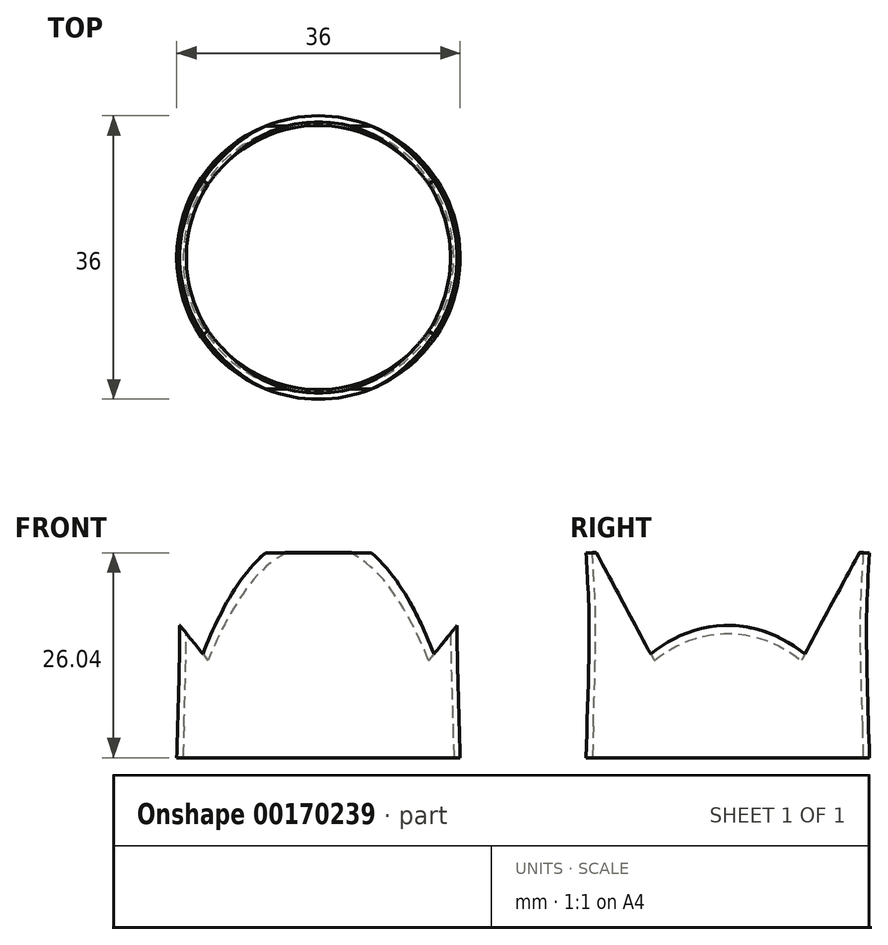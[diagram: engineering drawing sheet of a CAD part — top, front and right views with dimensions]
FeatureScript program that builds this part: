
annotation { "Feature Type Name" : "Feature", "Feature Type Description" : "" }
export const myFeature = defineFeature(function(context is Context, id is Id, definition is map)
    precondition{}
    {
        {
            assignVariable(context, id + "F0", {"name" : "cop", "anyValue" : 5});
        }
        {
            var Q0;
            Q0=qCreatedBy(makeId("Top.planeOp"),FACE);
            var sketch = newSketch(context, id + "F1", { "sketchPlane" : qUnion([Q0])});
            skCircle(sketch, "E0", {"center": v(0, 0) * mm, "radius": 16 * mm});
            skCircle(sketch, "E1.0", {"center": v(0, 0) * mm, "radius": 18 * mm});
            skSolve(sketch);
        }
        {
            var Q0;
            Q0=qCreatedBy(makeId("Front.planeOp"),FACE);
            var sketch = newSketch(context, id + "F2", { "sketchPlane" : qUnion([Q0])});
            skLineSegment(sketch, "E2.0", {"start": v(-18, 0) * mm, "end": v(18, 0) * mm});
            skLineSegment(sketch, "E3.0", {"start": v(-16, 0) * mm, "end": v(16, 0) * mm});
            skFitSpline(sketch, "E4", {"points": [v(18, 0) * mm, v(18, 26) * mm], "startDerivative": vector(-1.55, 51.63) * mm, "endDerivative": vector(1.55, 26.7) * mm});
            skFitSpline(sketch, "E5.0", {"points": [v(17.2, -0.02) * mm, v(17.07, 4.28) * mm, v(16.88, 10.72) * mm, v(16.78, 16.37) * mm, v(16.88, 20.5) * mm, v(17.07, 23.82) * mm, v(17.2, 26.05) * mm]});
            skLineSegment(sketch, "E6", {"start": v(17.2, 26.04) * mm, "end": v(18, 26) * mm});
            skLineSegment(sketch, "E7", {"start": v(17.14, 2) * mm, "end": v(16, 2) * mm});
            skLineSegment(sketch, "E8", {"start": v(16, 2) * mm, "end": v(16.56, 0) * mm});
            skLineSegment(sketch, "E9", {"start": v(16, 2) * mm, "end": v(16, 4) * mm});
            skLineSegment(sketch, "E10", {"start": v(16, 4) * mm, "end": v(17.08, 4) * mm});
            skSolve(sketch);
        }
        {
            var Q0;
            {var subQ0=sQuery(id+"F2.wireOp",EDGE,"E4");Q0=makeQuery(id+"F2.imprint","IMPRINT",FACE,{"disambiguationData":[TD([[makeQuery(id+"F2.imprint","IMPRINT",EDGE,{"derivedFrom":subQ0}),1.0]])]});}
            var Q1;
            {var subQ4=sQuery(id+"F2.wireOp",EDGE,"E7");Q1=makeQuery(id+"F2.imprint","IMPRINT",FACE,{"disambiguationData":[TD([[makeQuery(id+"F2.imprint","IMPRINT",EDGE,{"derivedFrom":subQ4}),1.0]])]});}
            var Q2;
            {var subQ0=sQuery(id+"F2.wireOp",EDGE,"E7");Q2=makeQuery(id+"F2.imprint","IMPRINT",FACE,{"disambiguationData":[TD([[makeQuery(id+"F2.imprint","IMPRINT",EDGE,{"derivedFrom":subQ0}),-1.0]])]});}
            var Q3;
            Q3=sQuery(id+"F1.wireOp",EDGE,"E0");
            revolve(context, id + "F3", {"entities" : qUnion([Q0, Q1, Q2]), "axis" : qUnion([Q3]), "revolveType" : RevolveType.FULL});
        }
        {
            var Q0;
            Q0=qCreatedBy(makeId("Top.planeOp"),FACE);
            cPlane(context, id + "F4", {"entities" : qUnion([Q0]), "cplaneType" : CPlaneType.OFFSET, "offset" : (getVariable(context, 'cop')) * mm, "oppositeDirection" : true, "width" : 150 * mm, "height" : 150 * mm});
        }
        {
            var Q0;
            Q0=qCreatedBy(id+"F4.planeOp",FACE);
            var sketch = newSketch(context, id + "F5", { "sketchPlane" : qUnion([Q0])});
            skCircle(sketch, "E11.0", {"center": v(0, 0) * mm, "radius": 16 * mm});
            skPoint(sketch, "E12.right.end.orphan", {"position": v(-0.75, 0.5) * mm});
            skPoint(sketch, "E12.bottom.end.orphan", {"position": v(-0.75, -0.5) * mm});
            skPoint(sketch, "E12.left.end.orphan", {"position": v(0.75, 0.5) * mm});
            skPoint(sketch, "E12.left.start.orphan", {"position": v(0.75, -0.5) * mm});
            skSolve(sketch);
        }
        {
            var Q0;
            Q0=qCreatedBy(id+"F4.planeOp",FACE);
            cPlane(context, id + "F6", {"entities" : qUnion([Q0]), "cplaneType" : CPlaneType.OFFSET, "offset" : (100 - getVariable(context, 'cop')) * mm, "width" : 150 * mm, "height" : 150 * mm});
        }
        {
            var Q0;
            Q0=qCreatedBy(id+"F6.planeOp",FACE);
            var sketch = newSketch(context, id + "F7", { "sketchPlane" : qUnion([Q0])});
            skLineSegment(sketch, "E13.bottom", {"start": v(76.73, -51.16) * mm, "end": v(-76.73, -51.16) * mm});
            skLineSegment(sketch, "E13.top", {"start": v(76.73, 51.16) * mm, "end": v(-76.73, 51.16) * mm});
            skLineSegment(sketch, "E13.left", {"start": v(76.73, -51.16) * mm, "end": v(76.73, 51.16) * mm});
            skLineSegment(sketch, "E13.right", {"start": v(-76.73, -51.16) * mm, "end": v(-76.73, 51.16) * mm});
            skPoint(sketch, "E13.middle", {"position": v(0, 0) * mm});
            skSolve(sketch);
        }
        {
            var Q1;
            Q1=makeQuery(id+"F7.imprint","IMPRINT",FACE,{"disambiguationData":[TD([[makeQuery(id+"F7.imprint","IMPRINT",EDGE,{"derivedFrom":sQuery(id+"F7.wireOp",EDGE,"E13.bottom")}),-1.0]])]});
            var Q2;
            Q2=sQuery(id+"F5.wireOp",VERTEX,"E11.0.center");
            loft(context, id + "F8", {"operationType" : NewBodyOperationType.REMOVE, "sheetProfilesArray" : [{ "sheetProfileEntities" : qUnion([Q1]) }, { "sheetProfileEntities" : qUnion([Q2]) }]});
        }
    });
